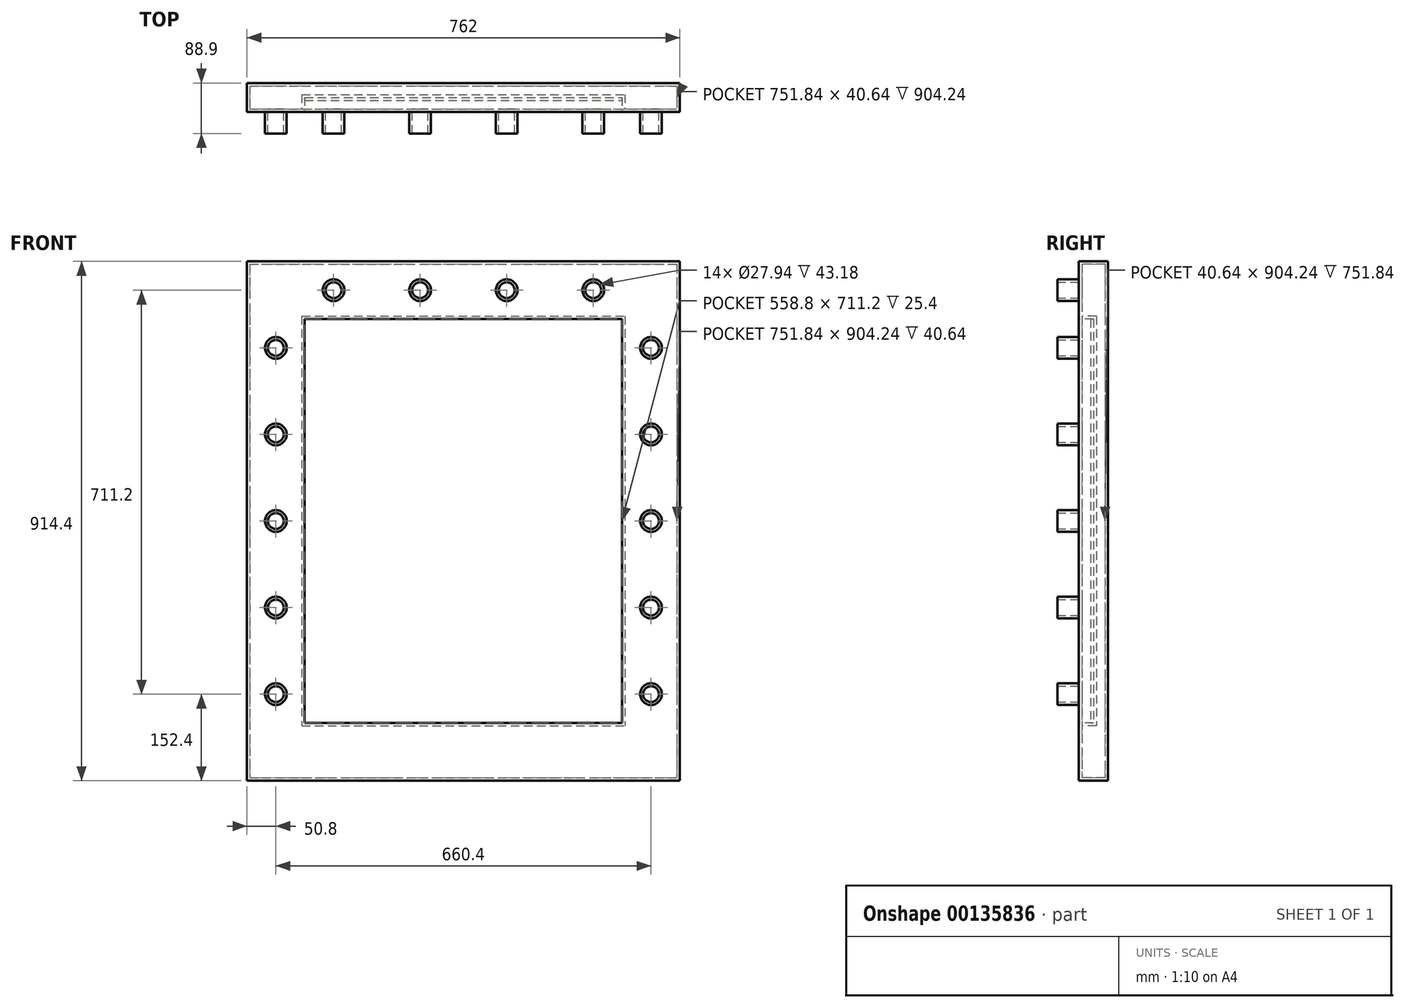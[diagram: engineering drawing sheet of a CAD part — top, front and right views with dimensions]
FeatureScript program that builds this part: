
annotation { "Feature Type Name" : "Feature", "Feature Type Description" : "" }
export const myFeature = defineFeature(function(context is Context, id is Id, definition is map)
    precondition{}
    {
        {
            var Q0;
            Q0=qCreatedBy(makeId("Top.planeOp"),FACE);
            var sketch = newSketch(context, id + "F0", { "sketchPlane" : qUnion([Q0])});
            skLineSegment(sketch, "E0.bottom", {"start": v(-381, 25.4) * mm, "end": v(381, 25.4) * mm});
            skLineSegment(sketch, "E0.top", {"start": v(-381, -25.4) * mm, "end": v(381, -25.4) * mm});
            skLineSegment(sketch, "E0.left", {"start": v(-381, 25.4) * mm, "end": v(-381, -25.4) * mm});
            skLineSegment(sketch, "E0.right", {"start": v(381, 25.4) * mm, "end": v(381, -25.4) * mm});
            skPoint(sketch, "E1.firstSnap0", {"position": v(0, 25.4) * mm});
            skLineSegment(sketch, "E1.bottom", {"start": v(0, 25.4) * mm, "end": v(0, 25.4) * mm});
            skLineSegment(sketch, "E1.top", {"start": v(-2.52, -25.4) * mm, "end": v(0, -25.4) * mm, "construction": true});
            skLineSegment(sketch, "E1.right", {"start": v(0, 25.4) * mm, "end": v(0, -25.4) * mm, "construction": true});
            skSolve(sketch);
        }
        {
            var Q0;
            Q0=makeQuery(id+"F0.imprint","IMPRINT",FACE,{"disambiguationData":[TD([[makeQuery(id+"F0.imprint","IMPRINT",EDGE,{"derivedFrom":sQuery(id+"F0.wireOp",EDGE,"E0.bottom")}),-1.0]])]});
            extrude(context, id + "F1", {"entities" : qUnion([Q0]), "endBound" : BoundingType.SYMMETRIC, "depth" : 914.4 * mm});
        }
        {
            var Q0;
            Q0=makeQuery(id+"F1.opExtrude","SWEPT_FACE",FACE,{"disambiguationData":[OSD([sQuery(id+"F0.wireOp",EDGE,"E0.top")])]});
            var sketch = newSketch(context, id + "F2", { "sketchPlane" : qUnion([Q0])});
            skLineSegment(sketch, "E2.bottom", {"start": v(-279.4, 355.6) * mm, "end": v(279.4, 355.6) * mm});
            skLineSegment(sketch, "E2.top", {"start": v(-279.4, -355.6) * mm, "end": v(279.4, -355.6) * mm});
            skLineSegment(sketch, "E2.left", {"start": v(-279.4, 355.6) * mm, "end": v(-279.4, -355.6) * mm});
            skLineSegment(sketch, "E2.right", {"start": v(279.4, 355.6) * mm, "end": v(279.4, -355.6) * mm});
            skSolve(sketch);
        }
        {
            var Q0;
            Q0=makeQuery(id+"F2.imprint","IMPRINT",FACE,{"disambiguationData":[TD([[makeQuery(id+"F2.imprint","IMPRINT",EDGE,{"derivedFrom":sQuery(id+"F2.wireOp",EDGE,"E2.bottom")}),-1.0]])]});
            extrude(context, id + "F3", {"entities" : qUnion([Q0]), "operationType" : NewBodyOperationType.REMOVE, "oppositeDirection" : true, "depth" : 25.4 * mm});
        }
        {
            var Q0;
            Q0=makeQuery(id+"F1.opExtrude","SWEPT_FACE",FACE,{"disambiguationData":[OSD([sQuery(id+"F0.wireOp",EDGE,"E0.top")])]});
            var sketch = newSketch(context, id + "F4", { "sketchPlane" : qUnion([Q0])});
            skLineSegment(sketch, "E3", {"start": v(-381, 406.4) * mm, "end": v(381, 406.4) * mm, "construction": true});
            skLineSegment(sketch, "E4", {"start": v(0, 457.2) * mm, "end": v(0, 355.6) * mm, "construction": true});
            skPoint(sketch, "E5", {"position": v(0, 406.4) * mm});
            skCircle(sketch, "E6", {"center": v(228.6, 406.4) * mm, "radius": 19.05 * mm});
            skLineSegment(sketch, "E7", {"start": v(-330.2, 457.2) * mm, "end": v(-330.2, -457.2) * mm, "construction": true});
            skLineSegment(sketch, "E8", {"start": v(330.2, 457.2) * mm, "end": v(330.2, -457.2) * mm, "construction": true});
            skLineSegment(sketch, "E9", {"start": v(-381, -406.4) * mm, "end": v(381, -406.4) * mm, "construction": true});
            skCircle(sketch, "E10", {"center": v(76.2, 406.4) * mm, "radius": 19.05 * mm});
            skCircle(sketch, "E11", {"center": v(-76.2, 406.4) * mm, "radius": 19.05 * mm});
            skCircle(sketch, "E12", {"center": v(-228.6, 406.4) * mm, "radius": 19.05 * mm});
            skCircle(sketch, "E13", {"center": v(-330.2, 304.8) * mm, "radius": 19.05 * mm});
            skCircle(sketch, "E14", {"center": v(-330.2, 152.4) * mm, "radius": 19.05 * mm});
            skCircle(sketch, "E15", {"center": v(-330.2, 0) * mm, "radius": 19.05 * mm});
            skCircle(sketch, "E16", {"center": v(-330.2, -152.4) * mm, "radius": 19.05 * mm});
            skCircle(sketch, "E17", {"center": v(-330.2, -304.8) * mm, "radius": 19.05 * mm});
            skCircle(sketch, "E18", {"center": v(330.2, 304.8) * mm, "radius": 19.05 * mm});
            skCircle(sketch, "E19", {"center": v(330.2, 152.4) * mm, "radius": 19.05 * mm});
            skCircle(sketch, "E20", {"center": v(330.2, 0) * mm, "radius": 19.05 * mm});
            skCircle(sketch, "E21", {"center": v(330.2, -152.4) * mm, "radius": 19.05 * mm});
            skCircle(sketch, "E22", {"center": v(330.2, -304.8) * mm, "radius": 19.05 * mm});
            skSolve(sketch);
        }
        {
            var Q0;
            Q0=makeQuery(id+"F4.imprint","IMPRINT",FACE,{"disambiguationData":[TD([[makeQuery(id+"F4.imprint","IMPRINT",EDGE,{"derivedFrom":sQuery(id+"F4.wireOp",EDGE,"E12")}),1.0]])]});
            var Q1;
            Q1=makeQuery(id+"F4.imprint","IMPRINT",FACE,{"disambiguationData":[TD([[makeQuery(id+"F4.imprint","IMPRINT",EDGE,{"derivedFrom":sQuery(id+"F4.wireOp",EDGE,"E13")}),1.0]])]});
            var Q2;
            Q2=makeQuery(id+"F4.imprint","IMPRINT",FACE,{"disambiguationData":[TD([[makeQuery(id+"F4.imprint","IMPRINT",EDGE,{"derivedFrom":sQuery(id+"F4.wireOp",EDGE,"E14")}),1.0]])]});
            var Q3;
            Q3=makeQuery(id+"F4.imprint","IMPRINT",FACE,{"disambiguationData":[TD([[makeQuery(id+"F4.imprint","IMPRINT",EDGE,{"derivedFrom":sQuery(id+"F4.wireOp",EDGE,"E15")}),1.0]])]});
            var Q4;
            Q4=makeQuery(id+"F4.imprint","IMPRINT",FACE,{"disambiguationData":[TD([[makeQuery(id+"F4.imprint","IMPRINT",EDGE,{"derivedFrom":sQuery(id+"F4.wireOp",EDGE,"E16")}),1.0]])]});
            var Q5;
            Q5=makeQuery(id+"F4.imprint","IMPRINT",FACE,{"disambiguationData":[TD([[makeQuery(id+"F4.imprint","IMPRINT",EDGE,{"derivedFrom":sQuery(id+"F4.wireOp",EDGE,"E17")}),1.0]])]});
            var Q6;
            Q6=makeQuery(id+"F4.imprint","IMPRINT",FACE,{"disambiguationData":[TD([[makeQuery(id+"F4.imprint","IMPRINT",EDGE,{"derivedFrom":sQuery(id+"F4.wireOp",EDGE,"JXyZejKC-K7BO-4Fv8-RiaZ-JVgBGUkwBhZs")}),1.0]])]});
            var Q7;
            Q7=makeQuery(id+"F4.imprint","IMPRINT",FACE,{"disambiguationData":[TD([[makeQuery(id+"F4.imprint","IMPRINT",EDGE,{"derivedFrom":sQuery(id+"F4.wireOp",EDGE,"MbmP8Rrr-r68R-278B-ERT5-FdHXGkjQpFYa")}),1.0]])]});
            var Q8;
            Q8=makeQuery(id+"F4.imprint","IMPRINT",FACE,{"disambiguationData":[TD([[makeQuery(id+"F4.imprint","IMPRINT",EDGE,{"derivedFrom":sQuery(id+"F4.wireOp",EDGE,"SGpKxNL5-Tin7-01z4-Y4BS-CkE7BABbUxkB")}),1.0]])]});
            var Q9;
            Q9=makeQuery(id+"F4.imprint","IMPRINT",FACE,{"disambiguationData":[TD([[makeQuery(id+"F4.imprint","IMPRINT",EDGE,{"derivedFrom":sQuery(id+"F4.wireOp",EDGE,"8Zy3xvhy-ydyA-PYAp-MW0r-a2Dy3dnRwZmV")}),1.0]])]});
            var Q10;
            Q10=makeQuery(id+"F4.imprint","IMPRINT",FACE,{"disambiguationData":[TD([[makeQuery(id+"F4.imprint","IMPRINT",EDGE,{"derivedFrom":sQuery(id+"F4.wireOp",EDGE,"E22")}),1.0]])]});
            var Q11;
            Q11=makeQuery(id+"F4.imprint","IMPRINT",FACE,{"disambiguationData":[TD([[makeQuery(id+"F4.imprint","IMPRINT",EDGE,{"derivedFrom":sQuery(id+"F4.wireOp",EDGE,"E21")}),1.0]])]});
            var Q12;
            Q12=makeQuery(id+"F4.imprint","IMPRINT",FACE,{"disambiguationData":[TD([[makeQuery(id+"F4.imprint","IMPRINT",EDGE,{"derivedFrom":sQuery(id+"F4.wireOp",EDGE,"E20")}),1.0]])]});
            var Q13;
            Q13=makeQuery(id+"F4.imprint","IMPRINT",FACE,{"disambiguationData":[TD([[makeQuery(id+"F4.imprint","IMPRINT",EDGE,{"derivedFrom":sQuery(id+"F4.wireOp",EDGE,"E19")}),1.0]])]});
            var Q14;
            Q14=makeQuery(id+"F4.imprint","IMPRINT",FACE,{"disambiguationData":[TD([[makeQuery(id+"F4.imprint","IMPRINT",EDGE,{"derivedFrom":sQuery(id+"F4.wireOp",EDGE,"E18")}),1.0]])]});
            var Q15;
            Q15=makeQuery(id+"F4.imprint","IMPRINT",FACE,{"disambiguationData":[TD([[makeQuery(id+"F4.imprint","IMPRINT",EDGE,{"derivedFrom":sQuery(id+"F4.wireOp",EDGE,"E11")}),1.0]])]});
            var Q16;
            Q16=makeQuery(id+"F4.imprint","IMPRINT",FACE,{"disambiguationData":[TD([[makeQuery(id+"F4.imprint","IMPRINT",EDGE,{"derivedFrom":sQuery(id+"F4.wireOp",EDGE,"E10")}),1.0]])]});
            var Q17;
            Q17=makeQuery(id+"F4.imprint","IMPRINT",FACE,{"disambiguationData":[TD([[makeQuery(id+"F4.imprint","IMPRINT",EDGE,{"derivedFrom":sQuery(id+"F4.wireOp",EDGE,"E6")}),1.0]])]});
            extrude(context, id + "F5", {"entities" : qUnion([Q0, Q1, Q2, Q3, Q4, Q5, Q6, Q7, Q8, Q9, Q10, Q11, Q12, Q13, Q14, Q15, Q16, Q17]), "operationType" : NewBodyOperationType.ADD, "depth" : 38.1 * mm});
        }
        {
            var Q0;
            Q0=makeQuery(id+"F5.opExtrude","CAP_FACE",FACE,{"disambiguationData":[OSD([sQuery(id+"F4.wireOp",EDGE,"E13")])],"isStart":false});
            var Q1;
            Q1=makeQuery(id+"F5.opExtrude","CAP_FACE",FACE,{"disambiguationData":[OSD([sQuery(id+"F4.wireOp",EDGE,"E14")])],"isStart":false});
            var Q2;
            Q2=makeQuery(id+"F5.opExtrude","CAP_FACE",FACE,{"disambiguationData":[OSD([sQuery(id+"F4.wireOp",EDGE,"E12")])],"isStart":false});
            var Q3;
            Q3=makeQuery(id+"F5.opExtrude","CAP_FACE",FACE,{"disambiguationData":[OSD([sQuery(id+"F4.wireOp",EDGE,"E11")])],"isStart":false});
            var Q4;
            Q4=makeQuery(id+"F5.opExtrude","CAP_FACE",FACE,{"disambiguationData":[OSD([sQuery(id+"F4.wireOp",EDGE,"E10")])],"isStart":false});
            var Q5;
            Q5=makeQuery(id+"F5.opExtrude","CAP_FACE",FACE,{"disambiguationData":[OSD([sQuery(id+"F4.wireOp",EDGE,"E6")])],"isStart":false});
            var Q6;
            Q6=makeQuery(id+"F5.opExtrude","CAP_FACE",FACE,{"disambiguationData":[OSD([sQuery(id+"F4.wireOp",EDGE,"E18")])],"isStart":false});
            var Q7;
            Q7=makeQuery(id+"F5.opExtrude","CAP_FACE",FACE,{"disambiguationData":[OSD([sQuery(id+"F4.wireOp",EDGE,"E19")])],"isStart":false});
            var Q8;
            Q8=makeQuery(id+"F5.opExtrude","CAP_FACE",FACE,{"disambiguationData":[OSD([sQuery(id+"F4.wireOp",EDGE,"E20")])],"isStart":false});
            var Q9;
            Q9=makeQuery(id+"F5.opExtrude","CAP_FACE",FACE,{"disambiguationData":[OSD([sQuery(id+"F4.wireOp",EDGE,"E22")])],"isStart":false});
            var Q10;
            Q10=makeQuery(id+"F5.opExtrude","CAP_FACE",FACE,{"disambiguationData":[OSD([sQuery(id+"F4.wireOp",EDGE,"E21")])],"isStart":false});
            var Q11;
            Q11=makeQuery(id+"F5.opExtrude","CAP_FACE",FACE,{"disambiguationData":[OSD([sQuery(id+"F4.wireOp",EDGE,"8Zy3xvhy-ydyA-PYAp-MW0r-a2Dy3dnRwZmV")])],"isStart":false});
            var Q12;
            Q12=makeQuery(id+"F5.opExtrude","CAP_FACE",FACE,{"disambiguationData":[OSD([sQuery(id+"F4.wireOp",EDGE,"SGpKxNL5-Tin7-01z4-Y4BS-CkE7BABbUxkB")])],"isStart":false});
            var Q13;
            Q13=makeQuery(id+"F5.opExtrude","CAP_FACE",FACE,{"disambiguationData":[OSD([sQuery(id+"F4.wireOp",EDGE,"MbmP8Rrr-r68R-278B-ERT5-FdHXGkjQpFYa")])],"isStart":false});
            var Q14;
            Q14=makeQuery(id+"F5.opExtrude","CAP_FACE",FACE,{"disambiguationData":[OSD([sQuery(id+"F4.wireOp",EDGE,"JXyZejKC-K7BO-4Fv8-RiaZ-JVgBGUkwBhZs")])],"isStart":false});
            var Q15;
            Q15=makeQuery(id+"F5.opExtrude","CAP_FACE",FACE,{"disambiguationData":[OSD([sQuery(id+"F4.wireOp",EDGE,"E17")])],"isStart":false});
            var Q16;
            Q16=makeQuery(id+"F5.opExtrude","CAP_FACE",FACE,{"disambiguationData":[OSD([sQuery(id+"F4.wireOp",EDGE,"E16")])],"isStart":false});
            var Q17;
            Q17=makeQuery(id+"F5.opExtrude","CAP_FACE",FACE,{"disambiguationData":[OSD([sQuery(id+"F4.wireOp",EDGE,"E15")])],"isStart":false});
            shell(context, id + "F6", {"entities" : qUnion([Q0, Q1, Q2, Q3, Q4, Q5, Q6, Q7, Q8, Q9, Q10, Q11, Q12, Q13, Q14, Q15, Q16, Q17]), "thickness" : 5.08 * mm});
        }
        {
            var Q0;
            Q0=makeQuery(id+"F3.boolean.opBoolean","COPY",FACE,{"derivedFrom":makeQuery(id+"F3.opExtrude","CAP_FACE",FACE,{"disambiguationData":[OSD([sQuery(id+"F2.wireOp",EDGE,"E2.bottom"),sQuery(id+"F2.wireOp",EDGE,"E2.top"),sQuery(id+"F2.wireOp",EDGE,"E2.left"),sQuery(id+"F2.wireOp",EDGE,"E2.right")])],"isStart":false})});
            extrude(context, id + "F7", {"entities" : qUnion([Q0]), "depth" : 5.08 * mm});
        }
    });
